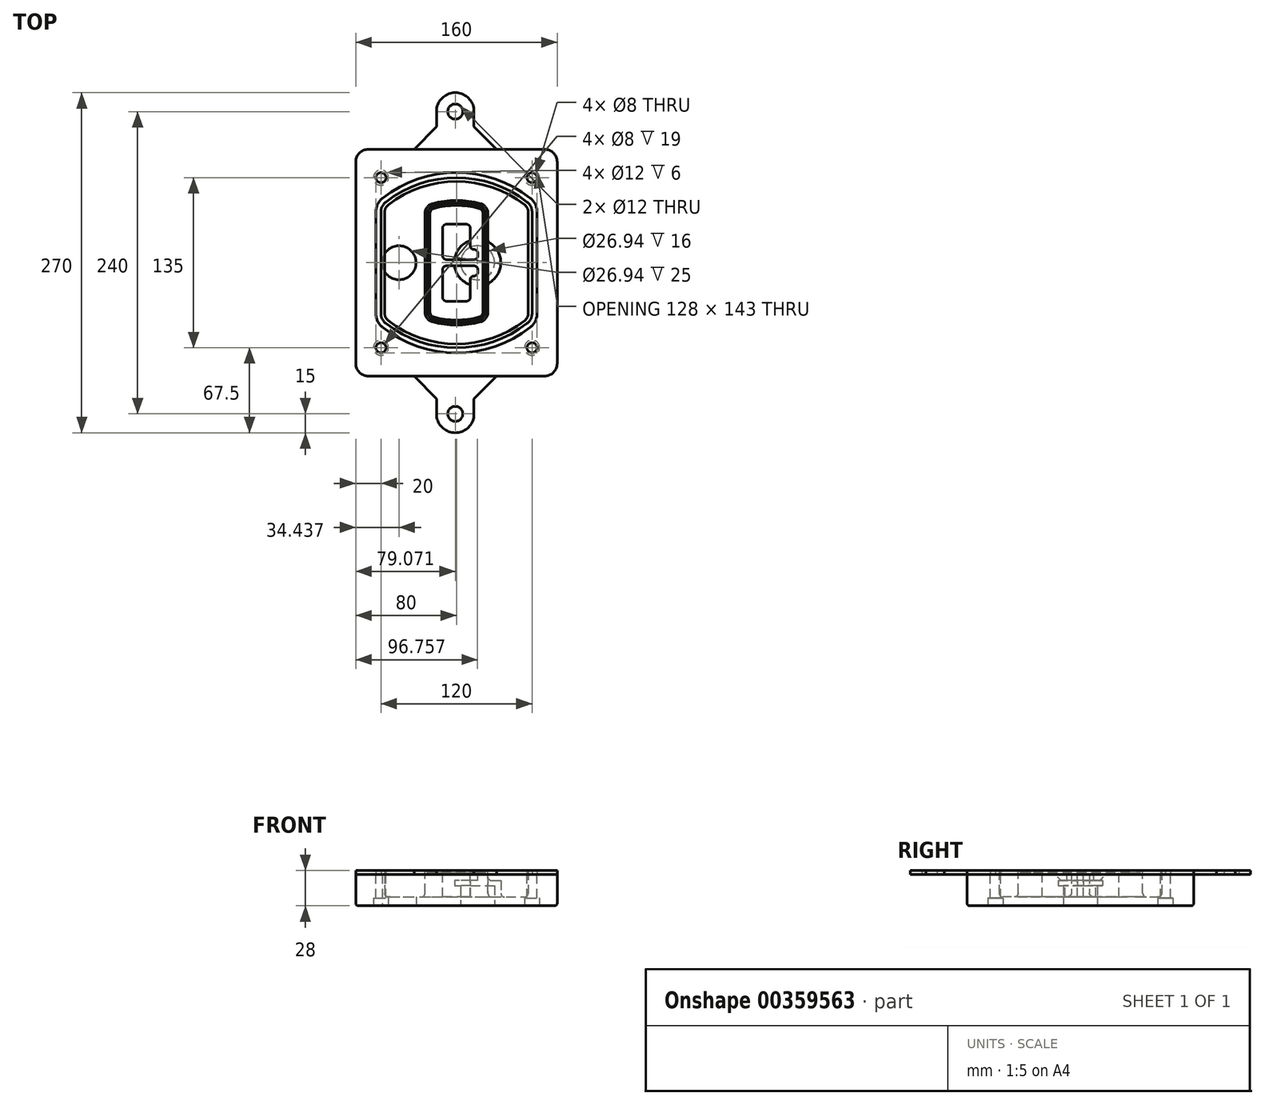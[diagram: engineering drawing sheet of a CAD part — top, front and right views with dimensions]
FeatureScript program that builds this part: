
annotation { "Feature Type Name" : "Feature", "Feature Type Description" : "" }
export const myFeature = defineFeature(function(context is Context, id is Id, definition is map)
    precondition{}
    {
        {
            var Q0;
            Q0=qCreatedBy(makeId("Top.planeOp"),FACE);
            var sketch = newSketch(context, id + "F0", { "sketchPlane" : qUnion([Q0])});
            skPoint(sketch, "E0.rect.middle", {"position": v(0, 0) * mm});
            skLineSegment(sketch, "E1.bottom", {"start": v(-70, -90) * mm, "end": v(70, -90) * mm});
            skLineSegment(sketch, "E1.top", {"start": v(-70, 90) * mm, "end": v(70, 90) * mm});
            skLineSegment(sketch, "E1.left", {"start": v(-80, -80) * mm, "end": v(-80, 80) * mm});
            skLineSegment(sketch, "E1.right", {"start": v(80, -80) * mm, "end": v(80, 80) * mm});
            skLineSegment(sketch, "E2", {"start": v(-80, 90) * mm, "end": v(80, -90) * mm, "construction": true});
            skLineSegment(sketch, "E3", {"start": v(80, 90) * mm, "end": v(-80, -90) * mm, "construction": true});
            skCircle(sketch, "E4", {"center": v(-60, 67.5) * mm, "radius": 4 * mm});
            skCircle(sketch, "E5", {"center": v(60, 67.5) * mm, "radius": 4 * mm});
            skCircle(sketch, "E6", {"center": v(60, -67.5) * mm, "radius": 4 * mm});
            skCircle(sketch, "E7", {"center": v(-60, -67.5) * mm, "radius": 4 * mm});
            skLineSegment(sketch, "E8", {"start": v(-60, 67.5) * mm, "end": v(60, 67.5) * mm, "construction": true});
            skLineSegment(sketch, "E9", {"start": v(60, 67.5) * mm, "end": v(60, -67.5) * mm, "construction": true});
            skLineSegment(sketch, "E10", {"start": v(60, -67.5) * mm, "end": v(-60, -67.5) * mm, "construction": true});
            skLineSegment(sketch, "E11", {"start": v(-60, -67.5) * mm, "end": v(-60, 67.5) * mm, "construction": true});
            skLineSegment(sketch, "E12", {"start": v(-60, 40.3) * mm, "end": v(-60, -40.3) * mm});
            skLineSegment(sketch, "E13", {"start": v(60, 40.3) * mm, "end": v(60, -40.3) * mm});
            skArc(sketch, "E14", {"start": v(56.15, 48.18) * mm, "mid": v(0, 67.5) * mm, "end": v(-56.15, 48.18) * mm});
            skArc(sketch, "E15", {"start": v(-56.15, -48.18) * mm, "mid": v(0, -67.5) * mm, "end": v(56.15, -48.18) * mm});
            skLineSegment(sketch, "E16", {"start": v(-60, 0) * mm, "end": v(60, 0) * mm, "construction": true});
            skPoint(sketch, "E17.visualSharp", {"position": v(-60, -45) * mm});
            skArc(sketch, "E17.filletArc", {"start": v(-60, -40.3) * mm, "mid": v(-58.99, -44.68) * mm, "end": v(-56.15, -48.18) * mm});
            skPoint(sketch, "E18.visualSharp", {"position": v(-60, 45) * mm});
            skArc(sketch, "E18.filletArc", {"start": v(-56.15, 48.18) * mm, "mid": v(-58.99, 44.68) * mm, "end": v(-60, 40.3) * mm});
            skPoint(sketch, "E19.visualSharp", {"position": v(60, 45) * mm});
            skArc(sketch, "E19.filletArc", {"start": v(60, 40.3) * mm, "mid": v(58.99, 44.68) * mm, "end": v(56.15, 48.18) * mm});
            skPoint(sketch, "E20.visualSharp", {"position": v(60, -45) * mm});
            skArc(sketch, "E20.filletArc", {"start": v(56.15, -48.18) * mm, "mid": v(58.99, -44.68) * mm, "end": v(60, -40.3) * mm});
            skPoint(sketch, "E21.visualSharp", {"position": v(-80, 90) * mm});
            skArc(sketch, "E21.filletArc", {"start": v(-70, 90) * mm, "mid": v(-77.07, 87.07) * mm, "end": v(-80, 80) * mm});
            skPoint(sketch, "E22.visualSharp", {"position": v(80, 90) * mm});
            skArc(sketch, "E22.filletArc", {"start": v(80, 80) * mm, "mid": v(77.07, 87.07) * mm, "end": v(70, 90) * mm});
            skPoint(sketch, "E23.visualSharp", {"position": v(80, -90) * mm});
            skArc(sketch, "E23.filletArc", {"start": v(70, -90) * mm, "mid": v(77.07, -87.07) * mm, "end": v(80, -80) * mm});
            skPoint(sketch, "E24.visualSharp", {"position": v(-80, -90) * mm});
            skArc(sketch, "E24.filletArc", {"start": v(-80, -80) * mm, "mid": v(-77.07, -87.07) * mm, "end": v(-70, -90) * mm});
            skArc(sketch, "E25.0", {"start": v(57, 40.3) * mm, "mid": v(56.3, 43.36) * mm, "end": v(54.3, 45.81) * mm});
            skLineSegment(sketch, "E25.1", {"start": v(57, 40.3) * mm, "end": v(57, -40.3) * mm});
            skArc(sketch, "E25.2", {"start": v(54.3, -45.81) * mm, "mid": v(56.3, -43.36) * mm, "end": v(57, -40.3) * mm});
            skArc(sketch, "E25.3", {"start": v(-54.3, -45.81) * mm, "mid": v(0, -64.5) * mm, "end": v(54.3, -45.81) * mm});
            skArc(sketch, "E25.4", {"start": v(-57, -40.3) * mm, "mid": v(-56.3, -43.36) * mm, "end": v(-54.3, -45.81) * mm});
            skArc(sketch, "E25.5", {"start": v(54.3, 45.81) * mm, "mid": v(0, 64.5) * mm, "end": v(-54.3, 45.81) * mm});
            skLineSegment(sketch, "E25.6", {"start": v(-57, 40.3) * mm, "end": v(-57, -40.3) * mm});
            skArc(sketch, "E25.7", {"start": v(-54.3, 45.81) * mm, "mid": v(-56.3, 43.36) * mm, "end": v(-57, 40.3) * mm});
            skArc(sketch, "E26.0", {"start": v(-58.62, 51.33) * mm, "mid": v(-62.58, 46.43) * mm, "end": v(-64, 40.3) * mm});
            skArc(sketch, "E26.1", {"start": v(58.62, 51.33) * mm, "mid": v(0, 71.5) * mm, "end": v(-58.62, 51.33) * mm});
            skArc(sketch, "E26.2", {"start": v(64, 40.3) * mm, "mid": v(62.58, 46.43) * mm, "end": v(58.62, 51.33) * mm});
            skLineSegment(sketch, "E26.3", {"start": v(64, 40.3) * mm, "end": v(64, -40.3) * mm});
            skArc(sketch, "E26.4", {"start": v(58.62, -51.33) * mm, "mid": v(62.58, -46.43) * mm, "end": v(64, -40.3) * mm});
            skLineSegment(sketch, "E26.5", {"start": v(-64, 40.3) * mm, "end": v(-64, -40.3) * mm});
            skArc(sketch, "E26.6", {"start": v(-58.62, -51.33) * mm, "mid": v(0, -71.5) * mm, "end": v(58.62, -51.33) * mm});
            skArc(sketch, "E26.7", {"start": v(-64, -40.3) * mm, "mid": v(-62.58, -46.43) * mm, "end": v(-58.62, -51.33) * mm});
            skSolve(sketch);
        }
        {
            var Q0;
            Q0=makeQuery(id+"F0.imprint","IMPRINT",FACE,{"disambiguationData":[TD([[makeQuery(id+"F0.imprint","IMPRINT",EDGE,{"derivedFrom":sQuery(id+"F0.wireOp",EDGE,"E1.bottom")}),1.0]])]});
            var Q1;
            Q1=makeQuery(id+"F0.imprint","IMPRINT",FACE,{"disambiguationData":[TD([[makeQuery(id+"F0.imprint","IMPRINT",EDGE,{"derivedFrom":sQuery(id+"F0.wireOp",EDGE,"E12")}),1.0]])]});
            var Q2;
            Q2=makeQuery(id+"F0.imprint","IMPRINT",FACE,{"disambiguationData":[TD([[makeQuery(id+"F0.imprint","IMPRINT",EDGE,{"derivedFrom":sQuery(id+"F0.wireOp",EDGE,"E25.0")}),1.0]])]});
            var Q3;
            Q3=makeQuery(id+"F0.imprint","IMPRINT",FACE,{"disambiguationData":[TD([[makeQuery(id+"F0.imprint","IMPRINT",EDGE,{"derivedFrom":sQuery(id+"F0.wireOp",EDGE,"E12")}),-1.0]])]});
            extrude(context, id + "F1", {"entities" : qUnion([Q0, Q1, Q2, Q3]), "oppositeDirection" : true, "depth" : 25 * mm});
        }
        {
            var Q0;
            Q0=makeQuery(id+"F0.imprint","IMPRINT",FACE,{"disambiguationData":[TD([[makeQuery(id+"F0.imprint","IMPRINT",EDGE,{"derivedFrom":sQuery(id+"F0.wireOp",EDGE,"E12")}),1.0]])]});
            extrude(context, id + "F2", {"entities" : qUnion([Q0]), "operationType" : NewBodyOperationType.ADD, "depth" : 3 * mm});
        }
        {
            var Q0;
            Q0=makeQuery(id+"F0.imprint","IMPRINT",FACE,{"disambiguationData":[TD([[makeQuery(id+"F0.imprint","IMPRINT",EDGE,{"derivedFrom":sQuery(id+"F0.wireOp",EDGE,"E25.0")}),1.0]])]});
            extrude(context, id + "F3", {"entities" : qUnion([Q0]), "operationType" : NewBodyOperationType.REMOVE, "oppositeDirection" : true, "depth" : 18 * mm});
        }
        {
            var Q0;
            Q0=makeQuery(id+"F2.opExtrude","CAP_FACE",FACE,{"disambiguationData":[OSD([sQuery(id+"F0.wireOp",EDGE,"E12"),sQuery(id+"F0.wireOp",EDGE,"E13"),sQuery(id+"F0.wireOp",EDGE,"E14"),sQuery(id+"F0.wireOp",EDGE,"E15"),sQuery(id+"F0.wireOp",EDGE,"E17.filletArc"),sQuery(id+"F0.wireOp",EDGE,"E18.filletArc"),sQuery(id+"F0.wireOp",EDGE,"E19.filletArc"),sQuery(id+"F0.wireOp",EDGE,"E20.filletArc"),sQuery(id+"F0.wireOp",EDGE,"E25.0"),sQuery(id+"F0.wireOp",EDGE,"E25.1"),sQuery(id+"F0.wireOp",EDGE,"E25.2"),sQuery(id+"F0.wireOp",EDGE,"E25.3"),sQuery(id+"F0.wireOp",EDGE,"E25.4"),sQuery(id+"F0.wireOp",EDGE,"E25.5"),sQuery(id+"F0.wireOp",EDGE,"E25.6"),sQuery(id+"F0.wireOp",EDGE,"E25.7")])],"isStart":false});
            var sketch = newSketch(context, id + "F4", { "sketchPlane" : qUnion([Q0])});
            skArc(sketch, "E27.0", {"start": v(-19.08, -46.97) * mm, "mid": v(0, -49.5) * mm, "end": v(19.08, -46.97) * mm});
            skArc(sketch, "E28.0", {"start": v(19.08, 46.97) * mm, "mid": v(0, 49.5) * mm, "end": v(-19.08, 46.97) * mm});
            skLineSegment(sketch, "E29", {"start": v(-25, 39.25) * mm, "end": v(-25, -39.25) * mm});
            skLineSegment(sketch, "E30", {"start": v(25, 39.25) * mm, "end": v(25, -39.25) * mm});
            skLineSegment(sketch, "E31", {"start": v(-25, 45.1) * mm, "end": v(25, 45.1) * mm, "construction": true});
            skLineSegment(sketch, "E32", {"start": v(-25, -45.1) * mm, "end": v(25, -45.1) * mm, "construction": true});
            skPoint(sketch, "E33.visualSharp", {"position": v(-25, 45.1) * mm});
            skArc(sketch, "E33.filletArc", {"start": v(-19.08, 46.97) * mm, "mid": v(-23.35, 44.11) * mm, "end": v(-25, 39.25) * mm});
            skPoint(sketch, "E34.visualSharp", {"position": v(25, 45.1) * mm});
            skArc(sketch, "E34.filletArc", {"start": v(25, 39.25) * mm, "mid": v(23.35, 44.11) * mm, "end": v(19.08, 46.97) * mm});
            skPoint(sketch, "E35.visualSharp", {"position": v(25, -45.1) * mm});
            skArc(sketch, "E35.filletArc", {"start": v(19.08, -46.97) * mm, "mid": v(23.35, -44.11) * mm, "end": v(25, -39.25) * mm});
            skPoint(sketch, "E36.visualSharp", {"position": v(-25, -45.1) * mm});
            skArc(sketch, "E36.filletArc", {"start": v(-25, -39.25) * mm, "mid": v(-23.35, -44.11) * mm, "end": v(-19.08, -46.97) * mm});
            skArc(sketch, "E37.0", {"start": v(54.3, 45.81) * mm, "mid": v(0, 64.5) * mm, "end": v(-54.3, 45.81) * mm});
            skArc(sketch, "E37.1", {"start": v(-54.3, 45.81) * mm, "mid": v(-56.3, 43.36) * mm, "end": v(-57, 40.3) * mm});
            skLineSegment(sketch, "E37.2", {"start": v(-57, 40.3) * mm, "end": v(-57, -40.3) * mm});
            skArc(sketch, "E37.3", {"start": v(-57, -40.3) * mm, "mid": v(-56.3, -43.36) * mm, "end": v(-54.3, -45.81) * mm});
            skArc(sketch, "E37.4", {"start": v(-54.3, -45.81) * mm, "mid": v(0, -64.5) * mm, "end": v(54.3, -45.81) * mm});
            skArc(sketch, "E37.5", {"start": v(54.3, -45.81) * mm, "mid": v(56.3, -43.36) * mm, "end": v(57, -40.3) * mm});
            skLineSegment(sketch, "E37.6", {"start": v(57, 40.3) * mm, "end": v(57, -40.3) * mm});
            skArc(sketch, "E37.7", {"start": v(57, 40.3) * mm, "mid": v(56.3, 43.36) * mm, "end": v(54.3, 45.81) * mm});
            skLineSegment(sketch, "E38.0", {"start": v(23, 39.25) * mm, "end": v(23, -39.25) * mm});
            skArc(sketch, "E38.1", {"start": v(18.56, -45.04) * mm, "mid": v(21.76, -42.9) * mm, "end": v(23, -39.25) * mm});
            skArc(sketch, "E38.2", {"start": v(-18.56, -45.04) * mm, "mid": v(0, -47.5) * mm, "end": v(18.56, -45.04) * mm});
            skArc(sketch, "E38.3", {"start": v(-23, -39.25) * mm, "mid": v(-21.76, -42.9) * mm, "end": v(-18.56, -45.04) * mm});
            skLineSegment(sketch, "E38.4", {"start": v(-23, 39.25) * mm, "end": v(-23, -39.25) * mm});
            skArc(sketch, "E38.5", {"start": v(23, 39.25) * mm, "mid": v(21.76, 42.9) * mm, "end": v(18.56, 45.04) * mm});
            skArc(sketch, "E38.6", {"start": v(-18.56, 45.04) * mm, "mid": v(-21.76, 42.9) * mm, "end": v(-23, 39.25) * mm});
            skArc(sketch, "E38.7", {"start": v(18.56, 45.04) * mm, "mid": v(0, 47.5) * mm, "end": v(-18.56, 45.04) * mm});
            skArc(sketch, "E39.0", {"start": v(21, 39.25) * mm, "mid": v(20.18, 41.68) * mm, "end": v(18.04, 43.1) * mm});
            skLineSegment(sketch, "E39.1", {"start": v(21, 39.25) * mm, "end": v(21, -39.25) * mm});
            skArc(sketch, "E39.2", {"start": v(18.04, -43.1) * mm, "mid": v(20.18, -41.68) * mm, "end": v(21, -39.25) * mm});
            skArc(sketch, "E39.3", {"start": v(-18.04, -43.1) * mm, "mid": v(0, -45.5) * mm, "end": v(18.04, -43.1) * mm});
            skArc(sketch, "E39.4", {"start": v(-21, -39.25) * mm, "mid": v(-20.18, -41.68) * mm, "end": v(-18.04, -43.1) * mm});
            skArc(sketch, "E39.5", {"start": v(18.04, 43.1) * mm, "mid": v(0, 45.5) * mm, "end": v(-18.04, 43.1) * mm});
            skLineSegment(sketch, "E39.6", {"start": v(-21, 39.25) * mm, "end": v(-21, -39.25) * mm});
            skArc(sketch, "E39.7", {"start": v(-18.04, 43.1) * mm, "mid": v(-20.18, 41.68) * mm, "end": v(-21, 39.25) * mm});
            skLineSegment(sketch, "E40", {"start": v(-25, 0) * mm, "end": v(25, 0) * mm, "construction": true});
            skLineSegment(sketch, "E41", {"start": v(-11, 5.5) * mm, "end": v(-11, 27.5) * mm});
            skLineSegment(sketch, "E42", {"start": v(-8, 30.5) * mm, "end": v(8, 30.5) * mm});
            skLineSegment(sketch, "E43", {"start": v(11, 27.5) * mm, "end": v(11, 13.5) * mm});
            skLineSegment(sketch, "E44", {"start": v(14, 10.5) * mm, "end": v(14, 10.5) * mm});
            skLineSegment(sketch, "E45", {"start": v(17, 7.5) * mm, "end": v(17, 5.5) * mm});
            skLineSegment(sketch, "E46", {"start": v(14, 2.5) * mm, "end": v(-8, 2.5) * mm});
            skPoint(sketch, "E47.visualSharp", {"position": v(-11, 30.5) * mm});
            skArc(sketch, "E47.filletArc", {"start": v(-8, 30.5) * mm, "mid": v(-10.12, 29.62) * mm, "end": v(-11, 27.5) * mm});
            skPoint(sketch, "E48.visualSharp", {"position": v(11, 30.5) * mm});
            skArc(sketch, "E48.filletArc", {"start": v(11, 27.5) * mm, "mid": v(10.12, 29.62) * mm, "end": v(8, 30.5) * mm});
            skPoint(sketch, "E49.visualSharp", {"position": v(11, 10.5) * mm});
            skArc(sketch, "E49.filletArc", {"start": v(11, 13.5) * mm, "mid": v(11.88, 11.38) * mm, "end": v(14, 10.5) * mm});
            skPoint(sketch, "E50.visualSharp", {"position": v(17, 10.5) * mm});
            skArc(sketch, "E50.filletArc", {"start": v(17, 7.5) * mm, "mid": v(16.12, 9.62) * mm, "end": v(14, 10.5) * mm});
            skPoint(sketch, "E51.visualSharp", {"position": v(17, 2.5) * mm});
            skArc(sketch, "E51.filletArc", {"start": v(14, 2.5) * mm, "mid": v(16.12, 3.38) * mm, "end": v(17, 5.5) * mm});
            skPoint(sketch, "E52.visualSharp", {"position": v(-11, 2.5) * mm});
            skArc(sketch, "E52.filletArc", {"start": v(-11, 5.5) * mm, "mid": v(-10.12, 3.38) * mm, "end": v(-8, 2.5) * mm});
            skLineSegment(sketch, "E53.0.MirrorCS", {"start": v(14, -2.5) * mm, "end": v(-8, -2.5) * mm});
            skArc(sketch, "E54.0.MirrorCS", {"start": v(-11, -5.5) * mm, "mid": v(-10.12, -3.38) * mm, "end": v(-8, -2.5) * mm});
            skLineSegment(sketch, "E55.0.MirrorCS", {"start": v(-11, -5.5) * mm, "end": v(-11, -27.5) * mm});
            skArc(sketch, "E56.0.MirrorCS", {"start": v(-8, -30.5) * mm, "mid": v(-10.12, -29.62) * mm, "end": v(-11, -27.5) * mm});
            skLineSegment(sketch, "E57.0.MirrorCS", {"start": v(-8, -30.5) * mm, "end": v(8, -30.5) * mm});
            skArc(sketch, "E58.0.MirrorCS", {"start": v(11, -27.5) * mm, "mid": v(10.12, -29.62) * mm, "end": v(8, -30.5) * mm});
            skLineSegment(sketch, "E59.0.MirrorCS", {"start": v(11, -27.5) * mm, "end": v(11, -13.5) * mm});
            skArc(sketch, "E60.0.MirrorCS", {"start": v(11, -13.5) * mm, "mid": v(11.88, -11.38) * mm, "end": v(14, -10.5) * mm});
            skArc(sketch, "E61.0.MirrorCS", {"start": v(17, -7.5) * mm, "mid": v(16.12, -9.62) * mm, "end": v(14, -10.5) * mm});
            skLineSegment(sketch, "E62.0.MirrorCS", {"start": v(17, -7.5) * mm, "end": v(17, -5.5) * mm});
            skArc(sketch, "E63.0.MirrorCS", {"start": v(14, -2.5) * mm, "mid": v(16.12, -3.38) * mm, "end": v(17, -5.5) * mm});
            skSolve(sketch);
        }
        {
            var Q0;
            Q0=makeQuery(id+"F4.imprint","IMPRINT",FACE,{"disambiguationData":[TD([[makeQuery(id+"F4.imprint","IMPRINT",EDGE,{"derivedFrom":sQuery(id+"F4.wireOp",EDGE,"E27.0")}),1.0]])]});
            var Q1;
            Q1=makeQuery(id+"F4.imprint","IMPRINT",FACE,{"disambiguationData":[TD([[makeQuery(id+"F4.imprint","IMPRINT",EDGE,{"derivedFrom":sQuery(id+"F4.wireOp",EDGE,"E38.0")}),-1.0]])]});
            var Q2;
            Q2=makeQuery(id+"F4.imprint","IMPRINT",FACE,{"disambiguationData":[TD([[makeQuery(id+"F4.imprint","IMPRINT",EDGE,{"derivedFrom":sQuery(id+"F4.wireOp",EDGE,"E39.0")}),1.0]])]});
            extrude(context, id + "F5", {"entities" : qUnion([Q0, Q1, Q2]), "operationType" : NewBodyOperationType.ADD, "endBound" : BoundingType.UP_TO_NEXT, "oppositeDirection" : true, "depth" : 25 * mm});
        }
        {
            var Q0;
            Q0=makeQuery(id+"F4.imprint","IMPRINT",FACE,{"disambiguationData":[TD([[makeQuery(id+"F4.imprint","IMPRINT",EDGE,{"derivedFrom":sQuery(id+"F4.wireOp",EDGE,"E38.0")}),-1.0]])]});
            extrude(context, id + "F6", {"entities" : qUnion([Q0]), "operationType" : NewBodyOperationType.REMOVE, "oppositeDirection" : true, "depth" : 2 * mm});
        }
        {
            var Q0;
            Q0=makeQuery(id+"F1.opExtrude","CAP_FACE",FACE,{"disambiguationData":[OSD([sQuery(id+"F0.wireOp",EDGE,"E1.bottom"),sQuery(id+"F0.wireOp",EDGE,"E1.top"),sQuery(id+"F0.wireOp",EDGE,"E1.left"),sQuery(id+"F0.wireOp",EDGE,"E1.right"),sQuery(id+"F0.wireOp",EDGE,"E4"),sQuery(id+"F0.wireOp",EDGE,"E5"),sQuery(id+"F0.wireOp",EDGE,"E6"),sQuery(id+"F0.wireOp",EDGE,"E7"),sQuery(id+"F0.wireOp",EDGE,"E21.filletArc"),sQuery(id+"F0.wireOp",EDGE,"E22.filletArc"),sQuery(id+"F0.wireOp",EDGE,"E23.filletArc"),sQuery(id+"F0.wireOp",EDGE,"E24.filletArc")])],"isStart":false});
            var sketch = newSketch(context, id + "F7", { "sketchPlane" : qUnion([Q0])});
            skCircle(sketch, "E64", {"center": v(16.76, 0) * mm, "radius": 13.47 * mm});
            skCircle(sketch, "E65", {"center": v(-45.56, 0) * mm, "radius": 13.47 * mm});
            skLineSegment(sketch, "E66", {"start": v(80, 0) * mm, "end": v(-80, 0) * mm});
            skCircle(sketch, "E67", {"center": v(16.76, 0) * mm, "radius": 18.47 * mm});
            skCircle(sketch, "E68", {"center": v(60, -67.5) * mm, "radius": 6 * mm});
            skCircle(sketch, "E69", {"center": v(-60, -67.5) * mm, "radius": 6 * mm});
            skCircle(sketch, "E70", {"center": v(-60, 67.5) * mm, "radius": 6 * mm});
            skCircle(sketch, "E71", {"center": v(60, 67.5) * mm, "radius": 6 * mm});
            skSolve(sketch);
        }
        {
            var Q0;
            {var subQ1=sQuery(id+"F7.wireOp",EDGE,"E66");var subQ4=sQuery(id+"F7.wireOp",EDGE,"E64");var subQ6=makeQuery(id+"F7.imprint","INTERSECT",VERTEX,{"disambiguationData":[OD(0.0)],"derivedFrom":[subQ4,subQ1]});Q0=makeQuery(id+"F7.imprint","IMPRINT",FACE,{"disambiguationData":[TD([[makeQuery(id+"F7.imprint","IMPRINT",EDGE,{"disambiguationData":[TD([[subQ6,-1.0]])],"derivedFrom":subQ4}),-1.0]])]});}
            var Q1;
            {var subQ0=sQuery(id+"F7.wireOp",EDGE,"E66");var subQ1=sQuery(id+"F7.wireOp",EDGE,"E64");var subQ3=makeQuery(id+"F7.imprint","INTERSECT",VERTEX,{"disambiguationData":[OD(0.0)],"derivedFrom":[subQ1,subQ0]});Q1=makeQuery(id+"F7.imprint","IMPRINT",FACE,{"disambiguationData":[TD([[makeQuery(id+"F7.imprint","IMPRINT",EDGE,{"disambiguationData":[TD([[subQ3,-1.0]])],"derivedFrom":subQ1}),1.0]])]});}
            var Q2;
            {var subQ0=sQuery(id+"F7.wireOp",EDGE,"E66");var subQ1=sQuery(id+"F7.wireOp",EDGE,"E64");var subQ3=makeQuery(id+"F7.imprint","INTERSECT",VERTEX,{"disambiguationData":[OD(0.0)],"derivedFrom":[subQ1,subQ0]});Q2=makeQuery(id+"F7.imprint","IMPRINT",FACE,{"disambiguationData":[TD([[makeQuery(id+"F7.imprint","IMPRINT",EDGE,{"disambiguationData":[TD([[subQ3,1.0]])],"derivedFrom":subQ1}),1.0]])]});}
            var Q3;
            {var subQ1=sQuery(id+"F7.wireOp",EDGE,"E66");var subQ4=sQuery(id+"F7.wireOp",EDGE,"E64");var subQ6=makeQuery(id+"F7.imprint","INTERSECT",VERTEX,{"disambiguationData":[OD(0.0)],"derivedFrom":[subQ4,subQ1]});Q3=makeQuery(id+"F7.imprint","IMPRINT",FACE,{"disambiguationData":[TD([[makeQuery(id+"F7.imprint","IMPRINT",EDGE,{"disambiguationData":[TD([[subQ6,1.0]])],"derivedFrom":subQ4}),-1.0]])]});}
            extrude(context, id + "F8", {"entities" : qUnion([Q0, Q1, Q2, Q3]), "operationType" : NewBodyOperationType.ADD, "oppositeDirection" : true, "depth" : 20 * mm});
        }
        {
            var Q0;
            {var subQ0=sQuery(id+"F7.wireOp",EDGE,"E66");var subQ1=sQuery(id+"F7.wireOp",EDGE,"E64");var subQ3=makeQuery(id+"F7.imprint","INTERSECT",VERTEX,{"disambiguationData":[OD(0.0)],"derivedFrom":[subQ1,subQ0]});Q0=makeQuery(id+"F7.imprint","IMPRINT",FACE,{"disambiguationData":[TD([[makeQuery(id+"F7.imprint","IMPRINT",EDGE,{"disambiguationData":[TD([[subQ3,-1.0]])],"derivedFrom":subQ1}),1.0]])]});}
            var Q1;
            {var subQ0=sQuery(id+"F7.wireOp",EDGE,"E66");var subQ1=sQuery(id+"F7.wireOp",EDGE,"E64");var subQ3=makeQuery(id+"F7.imprint","INTERSECT",VERTEX,{"disambiguationData":[OD(0.0)],"derivedFrom":[subQ1,subQ0]});Q1=makeQuery(id+"F7.imprint","IMPRINT",FACE,{"disambiguationData":[TD([[makeQuery(id+"F7.imprint","IMPRINT",EDGE,{"disambiguationData":[TD([[subQ3,1.0]])],"derivedFrom":subQ1}),1.0]])]});}
            extrude(context, id + "F9", {"entities" : qUnion([Q0, Q1]), "operationType" : NewBodyOperationType.REMOVE, "oppositeDirection" : true, "depth" : 16 * mm});
        }
        {
            var Q0;
            {var subQ0=sQuery(id+"F7.wireOp",EDGE,"E66");var subQ1=sQuery(id+"F7.wireOp",EDGE,"E65");var subQ3=makeQuery(id+"F7.imprint","INTERSECT",VERTEX,{"disambiguationData":[OD(0.0)],"derivedFrom":[subQ1,subQ0]});Q0=makeQuery(id+"F7.imprint","IMPRINT",FACE,{"disambiguationData":[TD([[makeQuery(id+"F7.imprint","IMPRINT",EDGE,{"disambiguationData":[TD([[subQ3,-1.0]])],"derivedFrom":subQ1}),1.0]])]});}
            var Q1;
            {var subQ0=sQuery(id+"F7.wireOp",EDGE,"E66");var subQ1=sQuery(id+"F7.wireOp",EDGE,"E65");var subQ3=makeQuery(id+"F7.imprint","INTERSECT",VERTEX,{"disambiguationData":[OD(0.0)],"derivedFrom":[subQ1,subQ0]});Q1=makeQuery(id+"F7.imprint","IMPRINT",FACE,{"disambiguationData":[TD([[makeQuery(id+"F7.imprint","IMPRINT",EDGE,{"disambiguationData":[TD([[subQ3,1.0]])],"derivedFrom":subQ1}),1.0]])]});}
            extrude(context, id + "F10", {"entities" : qUnion([Q0, Q1]), "operationType" : NewBodyOperationType.REMOVE, "oppositeDirection" : true, "depth" : 25 * mm});
        }
        {
            var Q0;
            Q0=makeQuery(id+"F7.imprint","IMPRINT",FACE,{"disambiguationData":[TD([[makeQuery(id+"F7.imprint","IMPRINT",EDGE,{"derivedFrom":sQuery(id+"F7.wireOp",EDGE,"E68")}),1.0]])]});
            var Q1;
            Q1=makeQuery(id+"F7.imprint","IMPRINT",FACE,{"disambiguationData":[TD([[makeQuery(id+"F7.imprint","IMPRINT",EDGE,{"derivedFrom":makeQuery(id+"F1.opExtrude","CAP_EDGE",EDGE,{"disambiguationData":[OSD([sQuery(id+"F0.wireOp",EDGE,"E5")])],"isStart":false})}),-1.0]])]});
            var Q2;
            Q2=makeQuery(id+"F7.imprint","IMPRINT",FACE,{"disambiguationData":[TD([[makeQuery(id+"F7.imprint","IMPRINT",EDGE,{"derivedFrom":sQuery(id+"F7.wireOp",EDGE,"E69")}),1.0]])]});
            var Q3;
            Q3=makeQuery(id+"F7.imprint","IMPRINT",FACE,{"disambiguationData":[TD([[makeQuery(id+"F7.imprint","IMPRINT",EDGE,{"derivedFrom":makeQuery(id+"F1.opExtrude","CAP_EDGE",EDGE,{"disambiguationData":[OSD([sQuery(id+"F0.wireOp",EDGE,"E4")])],"isStart":false})}),-1.0]])]});
            var Q4;
            Q4=makeQuery(id+"F7.imprint","IMPRINT",FACE,{"disambiguationData":[TD([[makeQuery(id+"F7.imprint","IMPRINT",EDGE,{"derivedFrom":sQuery(id+"F7.wireOp",EDGE,"E70")}),1.0]])]});
            var Q5;
            Q5=makeQuery(id+"F7.imprint","IMPRINT",FACE,{"disambiguationData":[TD([[makeQuery(id+"F7.imprint","IMPRINT",EDGE,{"derivedFrom":makeQuery(id+"F1.opExtrude","CAP_EDGE",EDGE,{"disambiguationData":[OSD([sQuery(id+"F0.wireOp",EDGE,"E7")])],"isStart":false})}),-1.0]])]});
            var Q6;
            Q6=makeQuery(id+"F7.imprint","IMPRINT",FACE,{"disambiguationData":[TD([[makeQuery(id+"F7.imprint","IMPRINT",EDGE,{"derivedFrom":sQuery(id+"F7.wireOp",EDGE,"E71")}),1.0]])]});
            var Q7;
            Q7=makeQuery(id+"F7.imprint","IMPRINT",FACE,{"disambiguationData":[TD([[makeQuery(id+"F7.imprint","IMPRINT",EDGE,{"derivedFrom":makeQuery(id+"F1.opExtrude","CAP_EDGE",EDGE,{"disambiguationData":[OSD([sQuery(id+"F0.wireOp",EDGE,"E6")])],"isStart":false})}),-1.0]])]});
            extrude(context, id + "F11", {"entities" : qUnion([Q0, Q1, Q2, Q3, Q4, Q5, Q6, Q7]), "operationType" : NewBodyOperationType.REMOVE, "oppositeDirection" : true, "depth" : 6 * mm});
        }
        {
            var Q0;
            Q0=makeQuery(id+"F9.boolean.opBoolean","COPY",FACE,{"derivedFrom":makeQuery(id+"F9.opExtrude","CAP_FACE",FACE,{"disambiguationData":[OSD([sQuery(id+"F7.wireOp",EDGE,"E64")])],"isStart":false})});
            var sketch = newSketch(context, id + "F12", { "sketchPlane" : qUnion([Q0])});
            skArc(sketch, "E72.0", {"start": v(11, 17.55) * mm, "mid": v(2.57, 11.82) * mm, "end": v(-1.54, 2.5) * mm});
            skArc(sketch, "E72.1", {"start": v(-1.54, -2.5) * mm, "mid": v(2.57, -11.82) * mm, "end": v(11, -17.55) * mm});
            skLineSegment(sketch, "E73", {"start": v(-1.54, -2.5) * mm, "end": v(14, -2.5) * mm});
            skLineSegment(sketch, "E74.0", {"start": v(14, 2.5) * mm, "end": v(-1.54, 2.5) * mm});
            skArc(sketch, "E74.1", {"start": v(14, 2.5) * mm, "mid": v(16.12, 3.38) * mm, "end": v(17, 5.5) * mm});
            skLineSegment(sketch, "E74.2", {"start": v(17, 7.5) * mm, "end": v(17, 5.5) * mm});
            skArc(sketch, "E74.3", {"start": v(17, 7.5) * mm, "mid": v(16.12, 9.62) * mm, "end": v(14, 10.5) * mm});
            skArc(sketch, "E74.4", {"start": v(11, 13.5) * mm, "mid": v(11.88, 11.38) * mm, "end": v(14, 10.5) * mm});
            skLineSegment(sketch, "E74.5", {"start": v(11, 17.55) * mm, "end": v(11, 13.5) * mm});
            skLineSegment(sketch, "E74.7", {"start": v(14, -2.5) * mm, "end": v(-1.54, -2.5) * mm});
            skArc(sketch, "E74.8", {"start": v(14, -2.5) * mm, "mid": v(16.12, -3.38) * mm, "end": v(17, -5.5) * mm});
            skLineSegment(sketch, "E74.9", {"start": v(17, -7.5) * mm, "end": v(17, -5.5) * mm});
            skArc(sketch, "E74.10", {"start": v(17, -7.5) * mm, "mid": v(16.12, -9.62) * mm, "end": v(14, -10.5) * mm});
            skArc(sketch, "E74.11", {"start": v(11, -13.5) * mm, "mid": v(11.88, -11.38) * mm, "end": v(14, -10.5) * mm});
            skLineSegment(sketch, "E74.12", {"start": v(11, -17.55) * mm, "end": v(11, -13.5) * mm});
            skPoint(sketch, "E75.orphan", {"position": v(11, -27.5) * mm});
            skPoint(sketch, "E76.orphan", {"position": v(-8, -2.5) * mm});
            skPoint(sketch, "E77.orphan", {"position": v(-8, 2.5) * mm});
            skPoint(sketch, "E78.orphan", {"position": v(11, 27.5) * mm});
            skSolve(sketch);
        }
        {
            var Q0;
            {var subQ7=sQuery(id+"F12.wireOp",EDGE,"E72.0");var subQ14=sQuery(id+"F12.wireOp",EDGE,"E72.1");var subQ16=sQuery(id+"F12.wireOp",EDGE,"E74.1");var subQ18=sQuery(id+"F12.wireOp",EDGE,"E74.8");Q0=qUnion([makeQuery(id+"F12.imprint","IMPRINT",FACE,{"disambiguationData":[TD([[makeQuery(id+"F12.imprint","IMPRINT",EDGE,{"derivedFrom":subQ7}),1.0]])]}),makeQuery(id+"F12.imprint","IMPRINT",FACE,{"disambiguationData":[TD([[makeQuery(id+"F12.imprint","IMPRINT",EDGE,{"derivedFrom":subQ14}),1.0]])]}),makeQuery(id+"F12.imprint","IMPRINT",FACE,{"disambiguationData":[TD([[makeQuery(id+"F12.imprint","IMPRINT",EDGE,{"derivedFrom":subQ16}),1.0]])]}),makeQuery(id+"F12.imprint","IMPRINT",FACE,{"disambiguationData":[TD([[makeQuery(id+"F12.imprint","IMPRINT",EDGE,{"derivedFrom":subQ18}),-1.0]])]})]);}
            var Q1;
            Q1=makeQuery(id+"F5.boolean.opBoolean","SPLIT",FACE,{"disambiguationData":[TD([makeQuery(id+"F5.opExtrude","SWEPT_FACE",FACE,{"disambiguationData":[OSD([sQuery(id+"F4.wireOp",EDGE,"E41")])]})])],"derivedFrom":makeQuery(id+"F3.boolean.opBoolean","COPY",FACE,{"derivedFrom":makeQuery(id+"F3.opExtrude","CAP_FACE",FACE,{"disambiguationData":[OSD([sQuery(id+"F0.wireOp",EDGE,"E25.0"),sQuery(id+"F0.wireOp",EDGE,"E25.1"),sQuery(id+"F0.wireOp",EDGE,"E25.2"),sQuery(id+"F0.wireOp",EDGE,"E25.3"),sQuery(id+"F0.wireOp",EDGE,"E25.4"),sQuery(id+"F0.wireOp",EDGE,"E25.5"),sQuery(id+"F0.wireOp",EDGE,"E25.6"),sQuery(id+"F0.wireOp",EDGE,"E25.7")])],"isStart":false})})});
            extrude(context, id + "F13", {"entities" : qUnion([Q0]), "operationType" : NewBodyOperationType.REMOVE, "endBound" : BoundingType.UP_TO_SURFACE, "endBoundEntityFace" : qUnion([Q1]), "depth" : 25 * mm});
        }
        {
            var Q0;
            Q0=makeQuery(id+"F3.boolean.opBoolean","COPY",EDGE,{"derivedFrom":makeQuery(id+"F3.opExtrude","CAP_EDGE",EDGE,{"disambiguationData":[OSD([sQuery(id+"F0.wireOp",EDGE,"E25.6")])],"isStart":false})});
            var Q1;
            Q1=makeQuery(id+"F8.boolean.opBoolean","INTERSECT",EDGE,{"derivedFrom":[makeQuery(id+"F5.opExtrude","SWEPT_FACE",FACE,{"disambiguationData":[OSD([sQuery(id+"F4.wireOp",EDGE,"E30")])]}),makeQuery(id+"F8.opExtrude","CAP_FACE",FACE,{"disambiguationData":[OSD([sQuery(id+"F7.wireOp",EDGE,"E67")])],"isStart":false})]});
            var Q2;
            Q2=makeQuery(id+"F8.boolean.opBoolean","INTERSECT",EDGE,{"disambiguationData":[OD(1.0)],"derivedFrom":[makeQuery(id+"F5.opExtrude","SWEPT_FACE",FACE,{"disambiguationData":[OSD([sQuery(id+"F4.wireOp",EDGE,"E30")])]}),makeQuery(id+"F8.opExtrude","SWEPT_FACE",FACE,{"disambiguationData":[OSD([sQuery(id+"F7.wireOp",EDGE,"E67")])]})]});
            var Q3;
            {var subQ0=sQuery(id+"F4.wireOp",EDGE,"E30");Q3=makeQuery(id+"F8.boolean.opBoolean","SPLIT",EDGE,{"disambiguationData":[TD([makeQuery(id+"F5.opExtrude","SWEPT_FACE",FACE,{"disambiguationData":[OSD([sQuery(id+"F4.wireOp",EDGE,"E35.filletArc")])]})])],"derivedFrom":makeQuery(id+"F5.opExtrude","CAP_EDGE",EDGE,{"disambiguationData":[OSD([subQ0])],"isStart":false})});}
            var Q4;
            {var subQ0=sQuery(id+"F0.wireOp",EDGE,"E25.7");var subQ1=sQuery(id+"F0.wireOp",EDGE,"E25.1");var subQ2=sQuery(id+"F0.wireOp",EDGE,"E25.6");var subQ3=sQuery(id+"F0.wireOp",EDGE,"E25.5");var subQ4=sQuery(id+"F0.wireOp",EDGE,"E25.4");var subQ5=sQuery(id+"F0.wireOp",EDGE,"E25.0");var subQ6=sQuery(id+"F0.wireOp",EDGE,"E25.2");var subQ7=sQuery(id+"F0.wireOp",EDGE,"E25.3");Q4=makeQuery(id+"F8.boolean.opBoolean","INTERSECT",EDGE,{"derivedFrom":[makeQuery(id+"F5.boolean.opBoolean","SPLIT",FACE,{"disambiguationData":[TD([makeQuery(id+"F2.opExtrude","SWEPT_FACE",FACE,{"disambiguationData":[OSD([subQ5])]})])],"derivedFrom":makeQuery(id+"F3.boolean.opBoolean","COPY",FACE,{"derivedFrom":makeQuery(id+"F3.opExtrude","CAP_FACE",FACE,{"disambiguationData":[OSD([subQ5,subQ1,subQ6,subQ7,subQ4,subQ3,subQ2,subQ0])],"isStart":false})})}),makeQuery(id+"F8.opExtrude","SWEPT_FACE",FACE,{"disambiguationData":[OSD([sQuery(id+"F7.wireOp",EDGE,"E67")])]})]});}
            var Q5;
            Q5=makeQuery(id+"F8.boolean.opBoolean","INTERSECT",EDGE,{"disambiguationData":[OD(0.0)],"derivedFrom":[makeQuery(id+"F5.opExtrude","SWEPT_FACE",FACE,{"disambiguationData":[OSD([sQuery(id+"F4.wireOp",EDGE,"E30")])]}),makeQuery(id+"F8.opExtrude","SWEPT_FACE",FACE,{"disambiguationData":[OSD([sQuery(id+"F7.wireOp",EDGE,"E67")])]})]});
            fillet(context, id + "F14", {"entities" : qUnion([Q0, Q1, Q2, Q3, Q4, Q5]), "radius" : 3 * mm, "tangentPropagation" : true, "allowEdgeOverflow" : false});
        }
        {
            var Q0;
            Q0=makeQuery(id+"F1.opExtrude","CAP_EDGE",EDGE,{"disambiguationData":[OSD([sQuery(id+"F0.wireOp",EDGE,"E1.bottom")])],"isStart":false});
            fillet(context, id + "F15", {"entities" : qUnion([Q0]), "radius" : 2 * mm, "tangentPropagation" : true, "allowEdgeOverflow" : false});
        }
        {
            var Q0;
            {var subQ0=sQuery(id+"F0.wireOp",EDGE,"E21.filletArc");var subQ1=sQuery(id+"F0.wireOp",EDGE,"E7");var subQ2=sQuery(id+"F0.wireOp",EDGE,"E6");var subQ3=sQuery(id+"F0.wireOp",EDGE,"E5");var subQ4=sQuery(id+"F0.wireOp",EDGE,"E4");var subQ5=sQuery(id+"F0.wireOp",EDGE,"E22.filletArc");var subQ6=sQuery(id+"F0.wireOp",EDGE,"E1.bottom");var subQ7=sQuery(id+"F0.wireOp",EDGE,"E1.right");var subQ8=sQuery(id+"F0.wireOp",EDGE,"E1.top");var subQ9=sQuery(id+"F0.wireOp",EDGE,"E1.left");var subQ10=sQuery(id+"F0.wireOp",EDGE,"E23.filletArc");var subQ11=sQuery(id+"F0.wireOp",EDGE,"E24.filletArc");Q0=makeQuery(id+"F2.boolean.opBoolean","SPLIT",FACE,{"disambiguationData":[TD([makeQuery(id+"F1.opExtrude","SWEPT_FACE",FACE,{"disambiguationData":[OSD([subQ6])]})])],"derivedFrom":makeQuery(id+"F1.opExtrude","CAP_FACE",FACE,{"disambiguationData":[OSD([subQ6,subQ8,subQ9,subQ7,subQ4,subQ3,subQ2,subQ1,subQ0,subQ5,subQ10,subQ11])],"isStart":true})});}
            var sketch = newSketch(context, id + "F16", { "sketchPlane" : qUnion([Q0])});
            skLineSegment(sketch, "E79", {"start": v(-33.65, 90) * mm, "end": v(-15.65, 108) * mm});
            skLineSegment(sketch, "E80", {"start": v(31.8, 90) * mm, "end": v(13.8, 108) * mm});
            skLineSegment(sketch, "E81", {"start": v(13.8, 108) * mm, "end": v(13.8, 122.86) * mm});
            skLineSegment(sketch, "E82", {"start": v(-15.65, 108) * mm, "end": v(-15.65, 122.86) * mm});
            skLineSegment(sketch, "E83", {"start": v(-33.65, 90) * mm, "end": v(31.8, 90) * mm});
            skArc(sketch, "E84", {"start": v(13.8, 122.86) * mm, "mid": v(-0.93, 135) * mm, "end": v(-15.65, 122.86) * mm});
            skCircle(sketch, "E85", {"center": v(-0.93, 120) * mm, "radius": 6 * mm});
            skLineSegment(sketch, "E86", {"start": v(-0.93, 120) * mm, "end": v(0, 90) * mm, "construction": true});
            skLineSegment(sketch, "E87", {"start": v(-80, 0) * mm, "end": v(80, 0) * mm, "construction": true});
            skCircle(sketch, "E88.MirrorC", {"center": v(-0.93, -120) * mm, "radius": 6 * mm});
            skLineSegment(sketch, "E89.MirrorCS", {"start": v(-15.65, -108) * mm, "end": v(-15.65, -122.86) * mm});
            skLineSegment(sketch, "E90.MirrorCS", {"start": v(13.8, -108) * mm, "end": v(13.8, -122.86) * mm});
            skLineSegment(sketch, "E91.MirrorCS", {"start": v(-33.65, -90) * mm, "end": v(-15.65, -108) * mm});
            skLineSegment(sketch, "E92.MirrorCS", {"start": v(-33.65, -90) * mm, "end": v(31.8, -90) * mm});
            skLineSegment(sketch, "E93.MirrorCS", {"start": v(31.8, -90) * mm, "end": v(13.8, -108) * mm});
            skArc(sketch, "E94.MirrorCS", {"start": v(13.8, -122.86) * mm, "mid": v(-0.93, -135) * mm, "end": v(-15.65, -122.86) * mm});
            skLineSegment(sketch, "E95.MirrorCS", {"start": v(-0.93, -120) * mm, "end": v(0, -90) * mm, "construction": true});
            skSolve(sketch);
        }
        {
            var Q0;
            Q0 = qSketchRegion(id + "F16", true);
            var Q1;
            Q1=makeQuery(id+"F2.opExtrude","CAP_FACE",FACE,{"disambiguationData":[OSD([sQuery(id+"F0.wireOp",EDGE,"E12"),sQuery(id+"F0.wireOp",EDGE,"E13"),sQuery(id+"F0.wireOp",EDGE,"E14"),sQuery(id+"F0.wireOp",EDGE,"E15"),sQuery(id+"F0.wireOp",EDGE,"E17.filletArc"),sQuery(id+"F0.wireOp",EDGE,"E18.filletArc"),sQuery(id+"F0.wireOp",EDGE,"E19.filletArc"),sQuery(id+"F0.wireOp",EDGE,"E20.filletArc"),sQuery(id+"F0.wireOp",EDGE,"E25.0"),sQuery(id+"F0.wireOp",EDGE,"E25.1"),sQuery(id+"F0.wireOp",EDGE,"E25.2"),sQuery(id+"F0.wireOp",EDGE,"E25.3"),sQuery(id+"F0.wireOp",EDGE,"E25.4"),sQuery(id+"F0.wireOp",EDGE,"E25.5"),sQuery(id+"F0.wireOp",EDGE,"E25.6"),sQuery(id+"F0.wireOp",EDGE,"E25.7")])],"isStart":false});
            extrude(context, id + "F17", {"entities" : qUnion([Q0]), "endBound" : BoundingType.UP_TO_SURFACE, "endBoundEntityFace" : qUnion([Q1]), "depth" : 25 * mm});
        }
        {
            var Q0;
            Q0 = qSketchRegion(id + "F0", true);
            var Q1;
            Q1=makeQuery(id+"F2.opExtrude","CAP_FACE",FACE,{"disambiguationData":[OSD([sQuery(id+"F0.wireOp",EDGE,"E12"),sQuery(id+"F0.wireOp",EDGE,"E13"),sQuery(id+"F0.wireOp",EDGE,"E14"),sQuery(id+"F0.wireOp",EDGE,"E15"),sQuery(id+"F0.wireOp",EDGE,"E17.filletArc"),sQuery(id+"F0.wireOp",EDGE,"E18.filletArc"),sQuery(id+"F0.wireOp",EDGE,"E19.filletArc"),sQuery(id+"F0.wireOp",EDGE,"E20.filletArc"),sQuery(id+"F0.wireOp",EDGE,"E25.0"),sQuery(id+"F0.wireOp",EDGE,"E25.1"),sQuery(id+"F0.wireOp",EDGE,"E25.2"),sQuery(id+"F0.wireOp",EDGE,"E25.3"),sQuery(id+"F0.wireOp",EDGE,"E25.4"),sQuery(id+"F0.wireOp",EDGE,"E25.5"),sQuery(id+"F0.wireOp",EDGE,"E25.6"),sQuery(id+"F0.wireOp",EDGE,"E25.7")])],"isStart":false});
            extrude(context, id + "F18", {"entities" : qUnion([Q0]), "endBound" : BoundingType.UP_TO_SURFACE, "endBoundEntityFace" : qUnion([Q1]), "depth" : 25 * mm});
        }
    });
